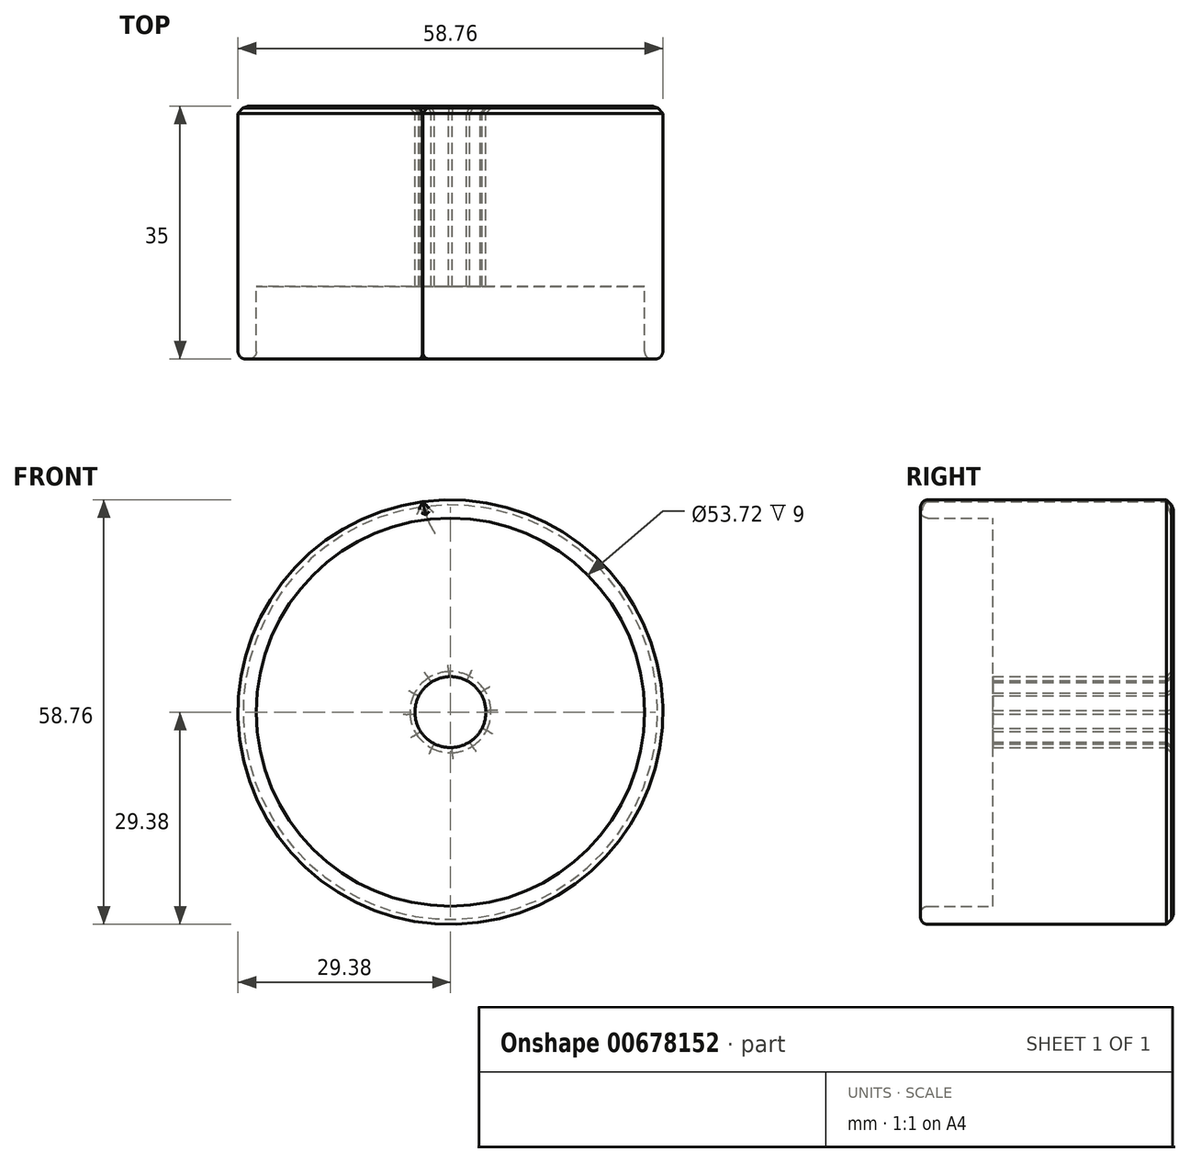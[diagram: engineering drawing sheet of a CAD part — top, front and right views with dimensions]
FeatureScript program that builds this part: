
annotation { "Feature Type Name" : "Feature", "Feature Type Description" : "" }
export const myFeature = defineFeature(function(context is Context, id is Id, definition is map)
    precondition{}
    {
        {
            var Q0;
            Q0=qCreatedBy(makeId("Front.planeOp"),FACE);
            var sketch = newSketch(context, id + "F0", { "sketchPlane" : qUnion([Q0])});
            skCircle(sketch, "E0", {"center": v(0, 0) * mm, "radius": 26.86 * mm});
            skCircle(sketch, "E1", {"center": v(0, 0) * mm, "radius": 29.35 * mm, "construction": true});
            skCircle(sketch, "E2", {"center": v(0, 0) * mm, "radius": 31.75 * mm, "construction": true});
            skLineSegment(sketch, "E3", {"start": v(0, 0) * mm, "end": v(0, 87.32) * mm, "construction": true});
            skLineSegment(sketch, "E4", {"start": v(0, 0) * mm, "end": v(-6.72, 102.52) * mm, "construction": true});
            skLineSegment(sketch, "E5", {"start": v(0, 29.35) * mm, "end": v(-57.61, 29.35) * mm, "construction": true});
            skLineSegment(sketch, "E6", {"start": v(0, 29.35) * mm, "end": v(-65.6, 5.47) * mm, "construction": true});
            skCircle(sketch, "E7", {"center": v(0, 0) * mm, "radius": 27.58 * mm, "construction": true});
            skCircle(sketch, "E8", {"center": v(0, 29.35) * mm, "radius": 14.6 * mm, "construction": true});
            skCircle(sketch, "E9", {"center": v(-13.72, 24.35) * mm, "radius": 14.6 * mm, "construction": true});
            skArc(sketch, "E10", {"start": v(0.66, 26.85) * mm, "mid": v(0.37, 28.1) * mm, "end": v(0, 29.35) * mm});
            skArc(sketch, "E11.MirrorCS", {"start": v(-3.83, 29.1) * mm, "mid": v(-4.9, 31.43) * mm, "end": v(-5.45, 33.94) * mm});
            skArc(sketch, "E12.MirrorCS", {"start": v(-3.83, 29.1) * mm, "mid": v(-3.03, 31.77) * mm, "end": v(-1.62, 34.19) * mm});
            skArc(sketch, "E13.MirrorCS", {"start": v(-4.16, 26.54) * mm, "mid": v(-4.04, 27.82) * mm, "end": v(-3.83, 29.1) * mm});
            skArc(sketch, "E14", {"start": v(0, 29.35) * mm, "mid": v(-1.18, 31.8) * mm, "end": v(-2.77, 34) * mm});
            skArc(sketch, "E15", {"start": v(-2.77, 34) * mm, "mid": v(-4.12, 34.47) * mm, "end": v(-5.45, 33.94) * mm});
            skCircle(sketch, "E16", {"center": v(0, 0) * mm, "radius": 29.38 * mm});
            skCircle(sketch, "E17", {"center": v(-0.14, 0.03) * mm, "radius": 5.05 * mm});
            skSolve(sketch);
        }
        {
            var Q0;
            {var subQ0=sQuery(id+"F0.wireOp",EDGE,"E0");var subQ1=makeQuery(id+"F0.imprint","INTERSECT",VERTEX,{"derivedFrom":[subQ0,sQuery(id+"F0.wireOp",EDGE,"E10")]});Q0=makeQuery(id+"F0.imprint","IMPRINT",FACE,{"disambiguationData":[TD([[makeQuery(id+"F0.imprint","IMPRINT",EDGE,{"disambiguationData":[TD([[subQ1,-1.0]])],"derivedFrom":subQ0}),1.0]])]});}
            var Q1;
            {var subQ1=sQuery(id+"F0.wireOp",EDGE,"E10");Q1=makeQuery(id+"F0.imprint","IMPRINT",FACE,{"disambiguationData":[TD([[makeQuery(id+"F0.imprint","IMPRINT",EDGE,{"derivedFrom":subQ1}),1.0]])]});}
            var Q2;
            {var subQ0=sQuery(id+"F0.wireOp",EDGE,"E14");var subQ1=sQuery(id+"F0.wireOp",EDGE,"E12.MirrorCS");var subQ2=makeQuery(id+"F0.imprint","INTERSECT",VERTEX,{"derivedFrom":[subQ1,subQ0]});Q2=makeQuery(id+"F0.imprint","IMPRINT",FACE,{"disambiguationData":[TD([[makeQuery(id+"F0.imprint","IMPRINT",EDGE,{"disambiguationData":[TD([[subQ2,1.0]])],"derivedFrom":subQ1}),-1.0]])]});}
            extrude(context, id + "F1", {"entities" : qUnion([Q0, Q1, Q2]), "depth" : 25 * mm, "offsetDistance" : 25 * mm});
        }
        {
            var Q0;
            Q0=makeQuery(id+"F1.opExtrude","SWEPT_BODY",BODY,{"disambiguationData":[OSD([sQuery(id+"F0.wireOp",EDGE,"E0"),sQuery(id+"F0.wireOp",EDGE,"E10"),sQuery(id+"F0.wireOp",EDGE,"E13.MirrorCS"),sQuery(id+"F0.wireOp",EDGE,"E12.MirrorCS"),sQuery(id+"F0.wireOp",EDGE,"E14"),sQuery(id+"F0.wireOp",EDGE,"E15")])]});
            var Q1;
            Q1=makeQuery(id+"F1.opExtrude","SWEPT_FACE",FACE,{"disambiguationData":[OSD([sQuery(id+"F0.wireOp",EDGE,"E0")])]});
            circularPattern(context, id + "F2", {"entities" : qUnion([Q0]), "axis" : qUnion([Q1]), "angle" : 360 * degree, "instanceCount" : 12, "equalSpace" : true});
        }
        {
            var Q0;
            Q0=makeQuery(id+"F0.imprint","IMPRINT",FACE,{"disambiguationData":[TD([[makeQuery(id+"F0.imprint","IMPRINT",EDGE,{"derivedFrom":sQuery(id+"F0.wireOp",EDGE,"E16")}),1.0]])]});
            extrude(context, id + "F3", {"entities" : qUnion([Q0]), "operationType" : NewBodyOperationType.ADD, "depth" : 35 * mm, "offsetDistance" : 25 * mm});
        }
        {
            var Q0;
            Q0=makeQuery(id+"F2.opPattern","COPY",FACE,{"derivedFrom":makeQuery(id+"F1.opExtrude","CAP_FACE",FACE,{"disambiguationData":[OSD([sQuery(id+"F0.wireOp",EDGE,"E0"),sQuery(id+"F0.wireOp",EDGE,"E10"),sQuery(id+"F0.wireOp",EDGE,"E13.MirrorCS"),sQuery(id+"F0.wireOp",EDGE,"E12.MirrorCS"),sQuery(id+"F0.wireOp",EDGE,"E14")])],"isStart":true}),"instanceName":"2"});
            chamfer(context, id + "F4", {"entities" : qUnion([Q0]), "width" : 1 * mm, "tangentPropagation" : true});
        }
        {
            var Q0;
            {var subQ0=sQuery(id+"F0.wireOp",EDGE,"E16");var subQ1=makeQuery(id+"F1.opExtrude","CAP_FACE",FACE,{"disambiguationData":[OSD([sQuery(id+"F0.wireOp",EDGE,"E0"),sQuery(id+"F0.wireOp",EDGE,"E10"),sQuery(id+"F0.wireOp",EDGE,"E13.MirrorCS"),sQuery(id+"F0.wireOp",EDGE,"E12.MirrorCS"),sQuery(id+"F0.wireOp",EDGE,"E14"),sQuery(id+"F0.wireOp",EDGE,"E15"),subQ0])],"isStart":true});Q0=makeQuery(id+"F3.boolean.opBoolean","MERGE",FACE,{"derivedFrom":[subQ1,makeQuery(id+"F2.opPattern","COPY",FACE,{"derivedFrom":subQ1,"instanceName":"1"}),makeQuery(id+"F2.opPattern","COPY",FACE,{"derivedFrom":subQ1,"instanceName":"2"}),makeQuery(id+"F2.opPattern","COPY",FACE,{"derivedFrom":subQ1,"instanceName":"3"}),makeQuery(id+"F2.opPattern","COPY",FACE,{"derivedFrom":subQ1,"instanceName":"4"}),makeQuery(id+"F2.opPattern","COPY",FACE,{"derivedFrom":subQ1,"instanceName":"5"}),makeQuery(id+"F2.opPattern","COPY",FACE,{"derivedFrom":subQ1,"instanceName":"6"}),makeQuery(id+"F2.opPattern","COPY",FACE,{"derivedFrom":subQ1,"instanceName":"7"}),makeQuery(id+"F2.opPattern","COPY",FACE,{"derivedFrom":subQ1,"instanceName":"8"}),makeQuery(id+"F2.opPattern","COPY",FACE,{"derivedFrom":subQ1,"instanceName":"9"}),makeQuery(id+"F2.opPattern","COPY",FACE,{"derivedFrom":subQ1,"instanceName":"10"}),makeQuery(id+"F2.opPattern","COPY",FACE,{"derivedFrom":subQ1,"instanceName":"11"}),makeQuery(id+"F2.opPattern","COPY",FACE,{"derivedFrom":subQ1,"instanceName":"12"}),makeQuery(id+"F2.opPattern","COPY",FACE,{"derivedFrom":subQ1,"instanceName":"13"}),makeQuery(id+"F2.opPattern","COPY",FACE,{"derivedFrom":subQ1,"instanceName":"14"}),makeQuery(id+"F2.opPattern","COPY",FACE,{"derivedFrom":subQ1,"instanceName":"15"}),makeQuery(id+"F2.opPattern","COPY",FACE,{"derivedFrom":subQ1,"instanceName":"16"}),makeQuery(id+"F2.opPattern","COPY",FACE,{"derivedFrom":subQ1,"instanceName":"17"}),makeQuery(id+"F2.opPattern","COPY",FACE,{"derivedFrom":subQ1,"instanceName":"18"}),makeQuery(id+"F2.opPattern","COPY",FACE,{"derivedFrom":subQ1,"instanceName":"19"}),makeQuery(id+"F2.opPattern","COPY",FACE,{"derivedFrom":subQ1,"instanceName":"20"}),makeQuery(id+"F2.opPattern","COPY",FACE,{"derivedFrom":subQ1,"instanceName":"21"}),makeQuery(id+"F2.opPattern","COPY",FACE,{"derivedFrom":subQ1,"instanceName":"22"}),makeQuery(id+"F2.opPattern","COPY",FACE,{"derivedFrom":subQ1,"instanceName":"23"}),makeQuery(id+"F3.opExtrude","CAP_FACE",FACE,{"disambiguationData":[OSD([subQ0,sQuery(id+"F0.wireOp",EDGE,"JNtdXsKn-sl94-sJaL-X6j9-ipqJ5UrsfOhM"),sQuery(id+"F0.wireOp",EDGE,"nhLlYziE-T9go-qMXb-Lngr-M2SgK2O0rp0T"),sQuery(id+"F0.wireOp",EDGE,"FmWoKXcW-Qzj9-4IRf-52Ky-pHPL5FFvMOR0"),sQuery(id+"F0.wireOp",EDGE,"DI1x3HvC-3bFb-MIyR-UmgX-l09uo7GKVcLs"),sQuery(id+"F0.wireOp",EDGE,"HNXKMdma-7YMK-hGZH-avgI-vMgkNqy3HRcJ"),sQuery(id+"F0.wireOp",EDGE,"5TuZqJqq-FCUH-1mfl-Rlqv-17RgC5mEEKbx"),sQuery(id+"F0.wireOp",EDGE,"hMIrZLfI-JfvP-B32Z-qgZj-gbDX4PTdaB8e")])],"isStart":true})]});}
            var Q1;
            Q1=makeQuery(id+"F2.opPattern","COPY",EDGE,{"derivedFrom":makeQuery(id+"F1.opExtrude","CAP_EDGE",EDGE,{"disambiguationData":[OSD([sQuery(id+"F0.wireOp",EDGE,"E0")])],"isStart":true}),"instanceName":"5"});
            chamfer(context, id + "F5", {"entities" : qUnion([Q0, Q1]), "width" : mm, "tangentPropagation" : true});
        }
        {
            var Q0;
            Q0=makeQuery(id+"F3.opExtrude","CAP_FACE",FACE,{"disambiguationData":[OSD([sQuery(id+"F0.wireOp",EDGE,"E16"),sQuery(id+"F0.wireOp",EDGE,"JNtdXsKn-sl94-sJaL-X6j9-ipqJ5UrsfOhM"),sQuery(id+"F0.wireOp",EDGE,"nhLlYziE-T9go-qMXb-Lngr-M2SgK2O0rp0T"),sQuery(id+"F0.wireOp",EDGE,"FmWoKXcW-Qzj9-4IRf-52Ky-pHPL5FFvMOR0"),sQuery(id+"F0.wireOp",EDGE,"DI1x3HvC-3bFb-MIyR-UmgX-l09uo7GKVcLs"),sQuery(id+"F0.wireOp",EDGE,"HNXKMdma-7YMK-hGZH-avgI-vMgkNqy3HRcJ"),sQuery(id+"F0.wireOp",EDGE,"5TuZqJqq-FCUH-1mfl-Rlqv-17RgC5mEEKbx"),sQuery(id+"F0.wireOp",EDGE,"hMIrZLfI-JfvP-B32Z-qgZj-gbDX4PTdaB8e")])],"isStart":false});
            fillet(context, id + "F6", {"entities" : qUnion([Q0]), "radius" : 1 * mm, "tangentPropagation" : true, "allowEdgeOverflow" : false});
        }
        {
            var Q0;
            {var subQ0=sQuery(id+"F0.wireOp",EDGE,"E16");var subQ1=makeQuery(id+"F1.opExtrude","CAP_FACE",FACE,{"disambiguationData":[OSD([sQuery(id+"F0.wireOp",EDGE,"E0"),sQuery(id+"F0.wireOp",EDGE,"E10"),sQuery(id+"F0.wireOp",EDGE,"E13.MirrorCS"),sQuery(id+"F0.wireOp",EDGE,"E12.MirrorCS"),sQuery(id+"F0.wireOp",EDGE,"E14"),sQuery(id+"F0.wireOp",EDGE,"E15"),subQ0])],"isStart":true});Q0=makeQuery(id+"F3.boolean.opBoolean","MERGE",FACE,{"derivedFrom":[subQ1,makeQuery(id+"F2.opPattern","COPY",FACE,{"derivedFrom":subQ1,"instanceName":"1"}),makeQuery(id+"F2.opPattern","COPY",FACE,{"derivedFrom":subQ1,"instanceName":"2"}),makeQuery(id+"F2.opPattern","COPY",FACE,{"derivedFrom":subQ1,"instanceName":"3"}),makeQuery(id+"F2.opPattern","COPY",FACE,{"derivedFrom":subQ1,"instanceName":"4"}),makeQuery(id+"F2.opPattern","COPY",FACE,{"derivedFrom":subQ1,"instanceName":"5"}),makeQuery(id+"F2.opPattern","COPY",FACE,{"derivedFrom":subQ1,"instanceName":"6"}),makeQuery(id+"F2.opPattern","COPY",FACE,{"derivedFrom":subQ1,"instanceName":"7"}),makeQuery(id+"F2.opPattern","COPY",FACE,{"derivedFrom":subQ1,"instanceName":"8"}),makeQuery(id+"F2.opPattern","COPY",FACE,{"derivedFrom":subQ1,"instanceName":"9"}),makeQuery(id+"F2.opPattern","COPY",FACE,{"derivedFrom":subQ1,"instanceName":"10"}),makeQuery(id+"F2.opPattern","COPY",FACE,{"derivedFrom":subQ1,"instanceName":"11"}),makeQuery(id+"F2.opPattern","COPY",FACE,{"derivedFrom":subQ1,"instanceName":"12"}),makeQuery(id+"F2.opPattern","COPY",FACE,{"derivedFrom":subQ1,"instanceName":"13"}),makeQuery(id+"F2.opPattern","COPY",FACE,{"derivedFrom":subQ1,"instanceName":"14"}),makeQuery(id+"F2.opPattern","COPY",FACE,{"derivedFrom":subQ1,"instanceName":"15"}),makeQuery(id+"F2.opPattern","COPY",FACE,{"derivedFrom":subQ1,"instanceName":"16"}),makeQuery(id+"F2.opPattern","COPY",FACE,{"derivedFrom":subQ1,"instanceName":"17"}),makeQuery(id+"F2.opPattern","COPY",FACE,{"derivedFrom":subQ1,"instanceName":"18"}),makeQuery(id+"F2.opPattern","COPY",FACE,{"derivedFrom":subQ1,"instanceName":"19"}),makeQuery(id+"F2.opPattern","COPY",FACE,{"derivedFrom":subQ1,"instanceName":"20"}),makeQuery(id+"F2.opPattern","COPY",FACE,{"derivedFrom":subQ1,"instanceName":"21"}),makeQuery(id+"F2.opPattern","COPY",FACE,{"derivedFrom":subQ1,"instanceName":"22"}),makeQuery(id+"F2.opPattern","COPY",FACE,{"derivedFrom":subQ1,"instanceName":"23"}),makeQuery(id+"F3.opExtrude","CAP_FACE",FACE,{"disambiguationData":[OSD([subQ0,sQuery(id+"F0.wireOp",EDGE,"JNtdXsKn-sl94-sJaL-X6j9-ipqJ5UrsfOhM"),sQuery(id+"F0.wireOp",EDGE,"nhLlYziE-T9go-qMXb-Lngr-M2SgK2O0rp0T"),sQuery(id+"F0.wireOp",EDGE,"FmWoKXcW-Qzj9-4IRf-52Ky-pHPL5FFvMOR0"),sQuery(id+"F0.wireOp",EDGE,"DI1x3HvC-3bFb-MIyR-UmgX-l09uo7GKVcLs"),sQuery(id+"F0.wireOp",EDGE,"HNXKMdma-7YMK-hGZH-avgI-vMgkNqy3HRcJ"),sQuery(id+"F0.wireOp",EDGE,"5TuZqJqq-FCUH-1mfl-Rlqv-17RgC5mEEKbx"),sQuery(id+"F0.wireOp",EDGE,"hMIrZLfI-JfvP-B32Z-qgZj-gbDX4PTdaB8e")])],"isStart":true})]});}
            fillet(context, id + "F7", {"entities" : qUnion([Q0]), "radius" : 1 * mm, "tangentPropagation" : true, "allowEdgeOverflow" : false});
        }
    });
